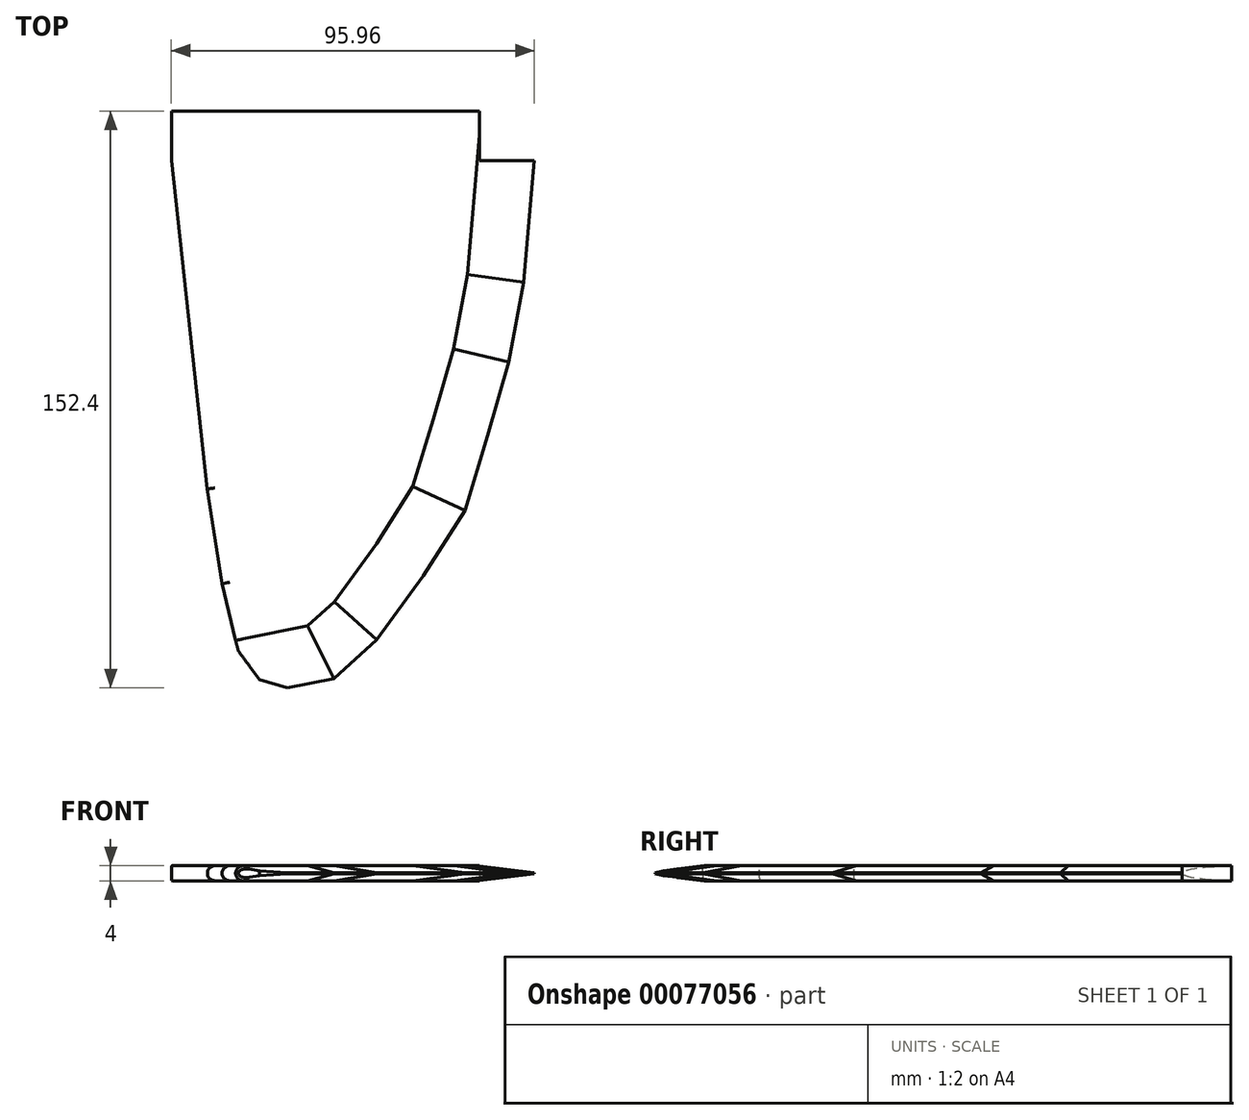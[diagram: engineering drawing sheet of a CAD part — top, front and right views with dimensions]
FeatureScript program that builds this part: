
annotation { "Feature Type Name" : "Feature", "Feature Type Description" : "" }
export const myFeature = defineFeature(function(context is Context, id is Id, definition is map)
    precondition{}
    {
        {
            var Q0;
            Q0=qCreatedBy(makeId("Top.planeOp"),FACE);
            var sketch = newSketch(context, id + "F0", { "sketchPlane" : qUnion([Q0])});
            skLineSegment(sketch, "E0", {"start": v(-99.84, 106.72) * mm, "end": v(-90.31, 19.93) * mm});
            skLineSegment(sketch, "E1", {"start": v(-90.31, 19.93) * mm, "end": v(-86.43, -5.12) * mm});
            skLineSegment(sketch, "E2", {"start": v(-86.43, -5.12) * mm, "end": v(-82.2, -22.75) * mm});
            skLineSegment(sketch, "E3", {"start": v(-82.2, -22.75) * mm, "end": v(-76.55, -30.52) * mm});
            skLineSegment(sketch, "E4", {"start": v(-76.55, -30.52) * mm, "end": v(-69.14, -32.63) * mm});
            skLineSegment(sketch, "E5", {"start": v(-69.14, -32.63) * mm, "end": v(-56.8, -30.16) * mm});
            skLineSegment(sketch, "E6", {"start": v(-56.8, -30.16) * mm, "end": v(-45.5, -19.93) * mm});
            skLineSegment(sketch, "E7", {"start": v(-45.5, -19.93) * mm, "end": v(-33.16, -3) * mm});
            skLineSegment(sketch, "E8", {"start": v(-33.16, -3) * mm, "end": v(-22.22, 14.29) * mm});
            skLineSegment(sketch, "E9", {"start": v(-22.22, 14.29) * mm, "end": v(-16.23, 34.04) * mm});
            skLineSegment(sketch, "E10", {"start": v(-16.23, 34.04) * mm, "end": v(-10.58, 53.45) * mm});
            skLineSegment(sketch, "E11", {"start": v(-10.58, 53.45) * mm, "end": v(-6.7, 74.61) * mm});
            skLineSegment(sketch, "E12", {"start": v(-6.7, 74.61) * mm, "end": v(-3.88, 106.72) * mm});
            skLineSegment(sketch, "E13", {"start": v(-3.88, 106.72) * mm, "end": v(-18.34, 106.72) * mm});
            skLineSegment(sketch, "E14", {"start": v(-18.34, 106.72) * mm, "end": v(-18.34, 119.77) * mm});
            skLineSegment(sketch, "E15", {"start": v(-18.34, 119.77) * mm, "end": v(-99.84, 119.77) * mm});
            skLineSegment(sketch, "E16", {"start": v(-99.84, 119.77) * mm, "end": v(-99.84, 106.72) * mm});
            skSolve(sketch);
        }
        {
            var Q0;
            Q0=makeQuery(id+"F0.imprint","IMPRINT",FACE,{"disambiguationData":[TD([[makeQuery(id+"F0.imprint","IMPRINT",EDGE,{"derivedFrom":sQuery(id+"F0.wireOp",EDGE,"E0")}),1.0]])]});
            extrude(context, id + "F1", {"entities" : qUnion([Q0]), "depth" : 2 * mm});
        }
        {
            var Q0;
            Q0=makeQuery(id+"F1.opExtrude","CAP_EDGE",EDGE,{"disambiguationData":[OSD([sQuery(id+"F0.wireOp",EDGE,"E12")])],"isStart":false});
            var Q1;
            Q1=makeQuery(id+"F1.opExtrude","CAP_EDGE",EDGE,{"disambiguationData":[OSD([sQuery(id+"F0.wireOp",EDGE,"E11")])],"isStart":false});
            var Q2;
            Q2=makeQuery(id+"F1.opExtrude","CAP_EDGE",EDGE,{"disambiguationData":[OSD([sQuery(id+"F0.wireOp",EDGE,"E10")])],"isStart":false});
            var Q3;
            Q3=makeQuery(id+"F1.opExtrude","CAP_EDGE",EDGE,{"disambiguationData":[OSD([sQuery(id+"F0.wireOp",EDGE,"E9")])],"isStart":false});
            var Q4;
            Q4=makeQuery(id+"F1.opExtrude","CAP_EDGE",EDGE,{"disambiguationData":[OSD([sQuery(id+"F0.wireOp",EDGE,"E8")])],"isStart":false});
            var Q5;
            Q5=makeQuery(id+"F1.opExtrude","CAP_EDGE",EDGE,{"disambiguationData":[OSD([sQuery(id+"F0.wireOp",EDGE,"E7")])],"isStart":false});
            var Q6;
            Q6=makeQuery(id+"F1.opExtrude","CAP_EDGE",EDGE,{"disambiguationData":[OSD([sQuery(id+"F0.wireOp",EDGE,"E6")])],"isStart":false});
            var Q7;
            Q7=makeQuery(id+"F1.opExtrude","CAP_EDGE",EDGE,{"disambiguationData":[OSD([sQuery(id+"F0.wireOp",EDGE,"E5")])],"isStart":false});
            chamfer(context, id + "F2", {"entities" : qUnion([Q0, Q1, Q2, Q3, Q4, Q5, Q6, Q7]), "chamferType" : ChamferType.OFFSET_ANGLE, "width" : 15 * mm, "oppositeDirection" : false, "angle" : 7 * degree, "tangentPropagation" : true});
        }
        {
            var Q0;
            Q0=makeQuery(id+"F1.opExtrude","CAP_EDGE",EDGE,{"disambiguationData":[OSD([sQuery(id+"F0.wireOp",EDGE,"E0")])],"isStart":false});
            var Q1;
            Q1=makeQuery(id+"F1.opExtrude","CAP_EDGE",EDGE,{"disambiguationData":[OSD([sQuery(id+"F0.wireOp",EDGE,"E1")])],"isStart":false});
            var Q2;
            Q2=makeQuery(id+"F1.opExtrude","CAP_EDGE",EDGE,{"disambiguationData":[OSD([sQuery(id+"F0.wireOp",EDGE,"E2")])],"isStart":false});
            var Q3;
            Q3=makeQuery(id+"F2.opChamfer","BLEND_EDGE",EDGE,{"blendedFrom":[makeQuery(id+"F1.opExtrude","CAP_EDGE",EDGE,{"disambiguationData":[OSD([sQuery(id+"F0.wireOp",EDGE,"E5")])],"isStart":false}),makeQuery(id+"F1.opExtrude","SWEPT_FACE",FACE,{"disambiguationData":[OSD([sQuery(id+"F0.wireOp",EDGE,"E2")])]})],"blendedInto":[makeQuery(id+"F1.opExtrude","SWEPT_FACE",FACE,{"disambiguationData":[OSD([sQuery(id+"F0.wireOp",EDGE,"E2")])]})]});
            fillet(context, id + "F3", {"entities" : qUnion([Q0, Q1, Q2, Q3]), "radius" : 2 * mm, "tangentPropagation" : true, "allowEdgeOverflow" : false});
        }
        {
            var Q0;
            Q0=makeQuery(id+"F1.opExtrude","SWEPT_BODY",BODY,{"disambiguationData":[OSD([sQuery(id+"F0.wireOp",EDGE,"E0"),sQuery(id+"F0.wireOp",EDGE,"E1"),sQuery(id+"F0.wireOp",EDGE,"E2"),sQuery(id+"F0.wireOp",EDGE,"E3"),sQuery(id+"F0.wireOp",EDGE,"E4"),sQuery(id+"F0.wireOp",EDGE,"E5"),sQuery(id+"F0.wireOp",EDGE,"E6"),sQuery(id+"F0.wireOp",EDGE,"E7"),sQuery(id+"F0.wireOp",EDGE,"E8"),sQuery(id+"F0.wireOp",EDGE,"E9"),sQuery(id+"F0.wireOp",EDGE,"E10"),sQuery(id+"F0.wireOp",EDGE,"E11"),sQuery(id+"F0.wireOp",EDGE,"E12"),sQuery(id+"F0.wireOp",EDGE,"E13"),sQuery(id+"F0.wireOp",EDGE,"E14"),sQuery(id+"F0.wireOp",EDGE,"E15"),sQuery(id+"F0.wireOp",EDGE,"E16")])]});
            var Q1;
            Q1=qCreatedBy(makeId("Top.planeOp"),FACE);
            mirror(context, id + "F4", {"operationType" : NewBodyOperationType.ADD, "entities" : qUnion([Q0]), "mirrorPlane" : qUnion([Q1])});
        }
    });
